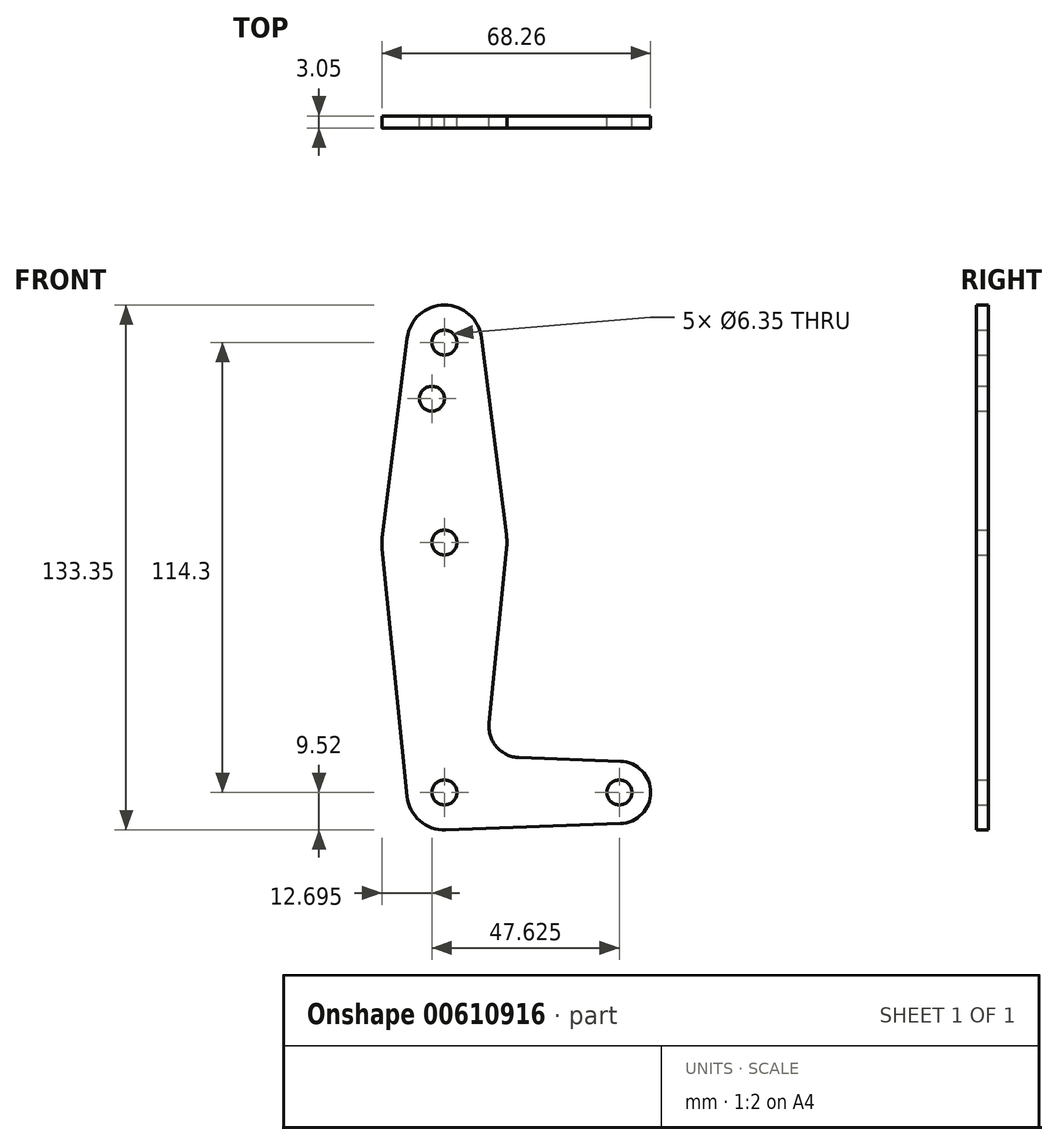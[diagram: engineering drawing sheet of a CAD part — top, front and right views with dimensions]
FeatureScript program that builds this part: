
annotation { "Feature Type Name" : "Feature", "Feature Type Description" : "" }
export const myFeature = defineFeature(function(context is Context, id is Id, definition is map)
    precondition{}
    {
        {
            var Q0;
            Q0=qCreatedBy(makeId("Front.planeOp"),FACE);
            var sketch = newSketch(context, id + "F0", { "sketchPlane" : qUnion([Q0])});
            skLineSegment(sketch, "E0", {"start": v(0, 114.3) * mm, "end": v(0, 0) * mm, "construction": true});
            skLineSegment(sketch, "E1", {"start": v(0, 0) * mm, "end": v(44.45, 0) * mm, "construction": true});
            skCircle(sketch, "E2", {"center": v(0, 114.3) * mm, "radius": 9.53 * mm});
            skCircle(sketch, "E3", {"center": v(0, 63.5) * mm, "radius": 15.88 * mm});
            skCircle(sketch, "E4", {"center": v(0, 0) * mm, "radius": 9.53 * mm});
            skCircle(sketch, "E5", {"center": v(44.45, 0) * mm, "radius": 7.94 * mm});
            skLineSegment(sketch, "E6", {"start": v(-9.45, 115.5) * mm, "end": v(-15.75, 65.48) * mm});
            skLineSegment(sketch, "E7", {"start": v(9.45, 115.5) * mm, "end": v(15.75, 65.48) * mm});
            skCircle(sketch, "E8", {"center": v(0, 114.3) * mm, "radius": 3.18 * mm});
            skCircle(sketch, "E9", {"center": v(-3.17, 100.03) * mm, "radius": 3.18 * mm});
            skCircle(sketch, "E10", {"center": v(0, 63.5) * mm, "radius": 3.18 * mm});
            skCircle(sketch, "E11", {"center": v(0, 0) * mm, "radius": 3.18 * mm});
            skCircle(sketch, "E12", {"center": v(44.45, 0) * mm, "radius": 3.18 * mm});
            skLineSegment(sketch, "E13", {"start": v(-15.8, 61.91) * mm, "end": v(-9.48, -0.95) * mm});
            skLineSegment(sketch, "E14", {"start": v(15.8, 61.91) * mm, "end": v(11.34, 17.6) * mm});
            skLineSegment(sketch, "E15", {"start": v(18.97, 8.85) * mm, "end": v(44.73, 7.93) * mm});
            skLineSegment(sketch, "E16", {"start": v(0.34, -9.52) * mm, "end": v(44.73, -7.93) * mm});
            skArc(sketch, "E17.filletArc", {"start": v(11.34, 17.6) * mm, "mid": v(13.26, 11.57) * mm, "end": v(18.97, 8.85) * mm});
            skSolve(sketch);
        }
        {
            var Q0;
            Q0 = qSketchRegion(id + "F0", true);
            extrude(context, id + "F1", {"entities" : qUnion([Q0]), "depth" : 3.05 * mm, "offsetDistance" : 25.4 * mm});
        }
    });
